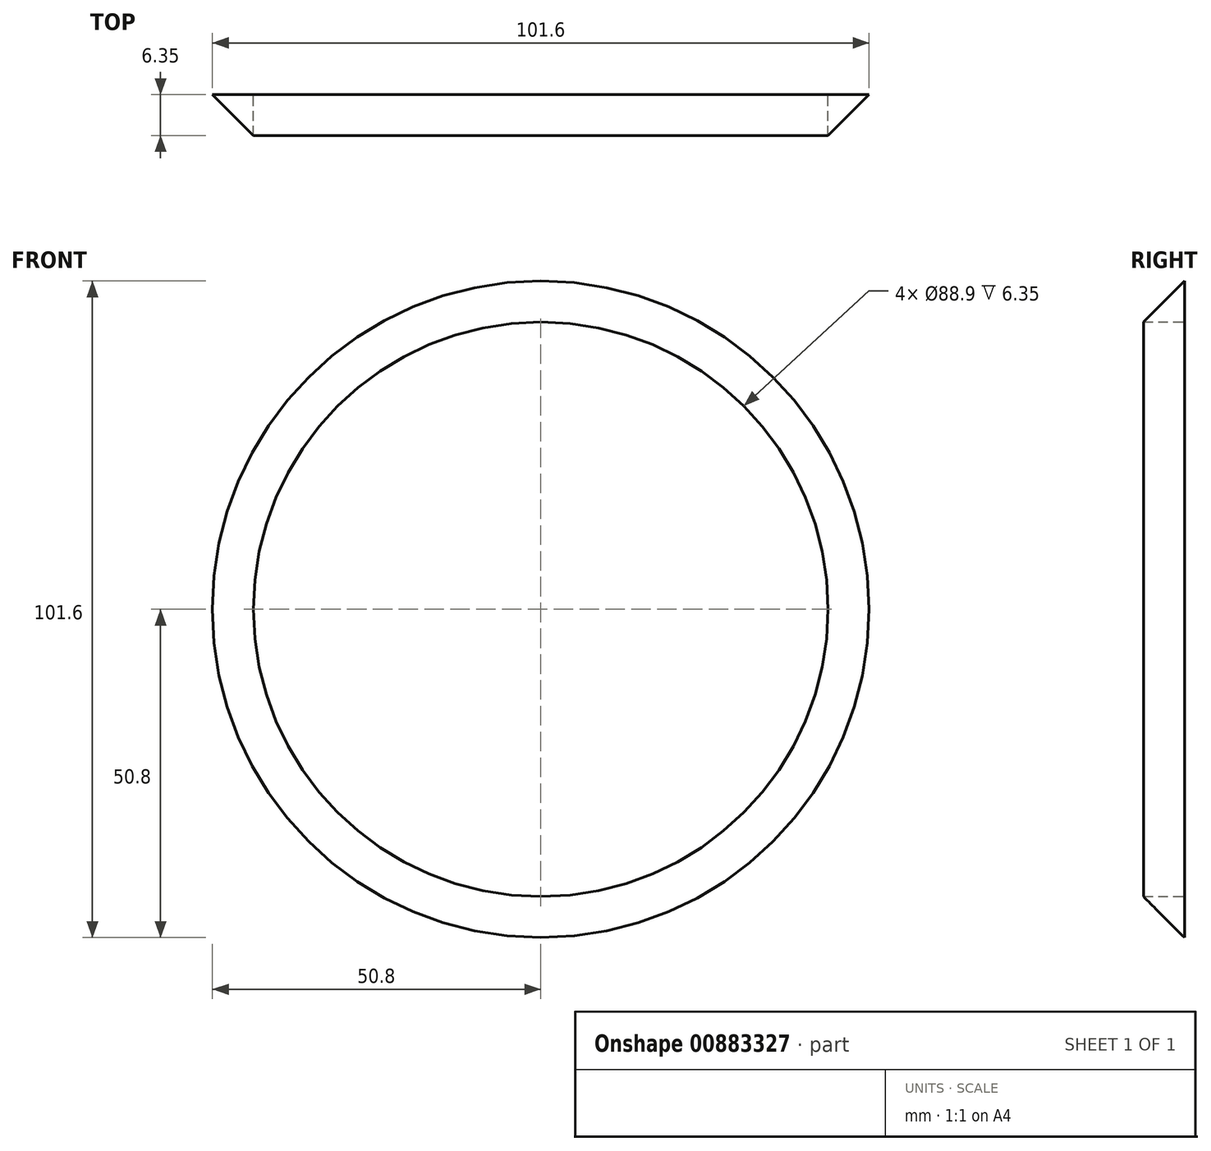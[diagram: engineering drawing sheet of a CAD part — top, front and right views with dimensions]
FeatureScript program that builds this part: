
annotation { "Feature Type Name" : "Feature", "Feature Type Description" : "" }
export const myFeature = defineFeature(function(context is Context, id is Id, definition is map)
    precondition{}
    {
        {
            var Q0;
            Q0=qCreatedBy(makeId("Front.planeOp"),FACE);
            var sketch = newSketch(context, id + "F0", { "sketchPlane" : qUnion([Q0])});
            skCircle(sketch, "E0", {"center": v(0, 0) * mm, "radius": 50.8 * mm});
            skCircle(sketch, "E1", {"center": v(0, 0) * mm, "radius": 44.45 * mm});
            skSolve(sketch);
        }
        {
            var Q0;
            Q0=makeQuery(id+"F0.imprint","IMPRINT",FACE,{"disambiguationData":[TD([[makeQuery(id+"F0.imprint","IMPRINT",EDGE,{"derivedFrom":sQuery(id+"F0.wireOp",EDGE,"E0")}),1.0]])]});
            extrude(context, id + "F1", {"entities" : qUnion([Q0]), "depth" : 6.35 * mm, "offsetDistance" : 25.4 * mm});
        }
        {
            var Q0;
            Q0=makeQuery(id+"F1.opExtrude","CAP_EDGE",EDGE,{"disambiguationData":[OSD([sQuery(id+"F0.wireOp",EDGE,"E0")])],"isStart":false});
            chamfer(context, id + "F2", {"entities" : qUnion([Q0]), "width" : 6.35 * mm, "tangentPropagation" : true});
        }
    });
